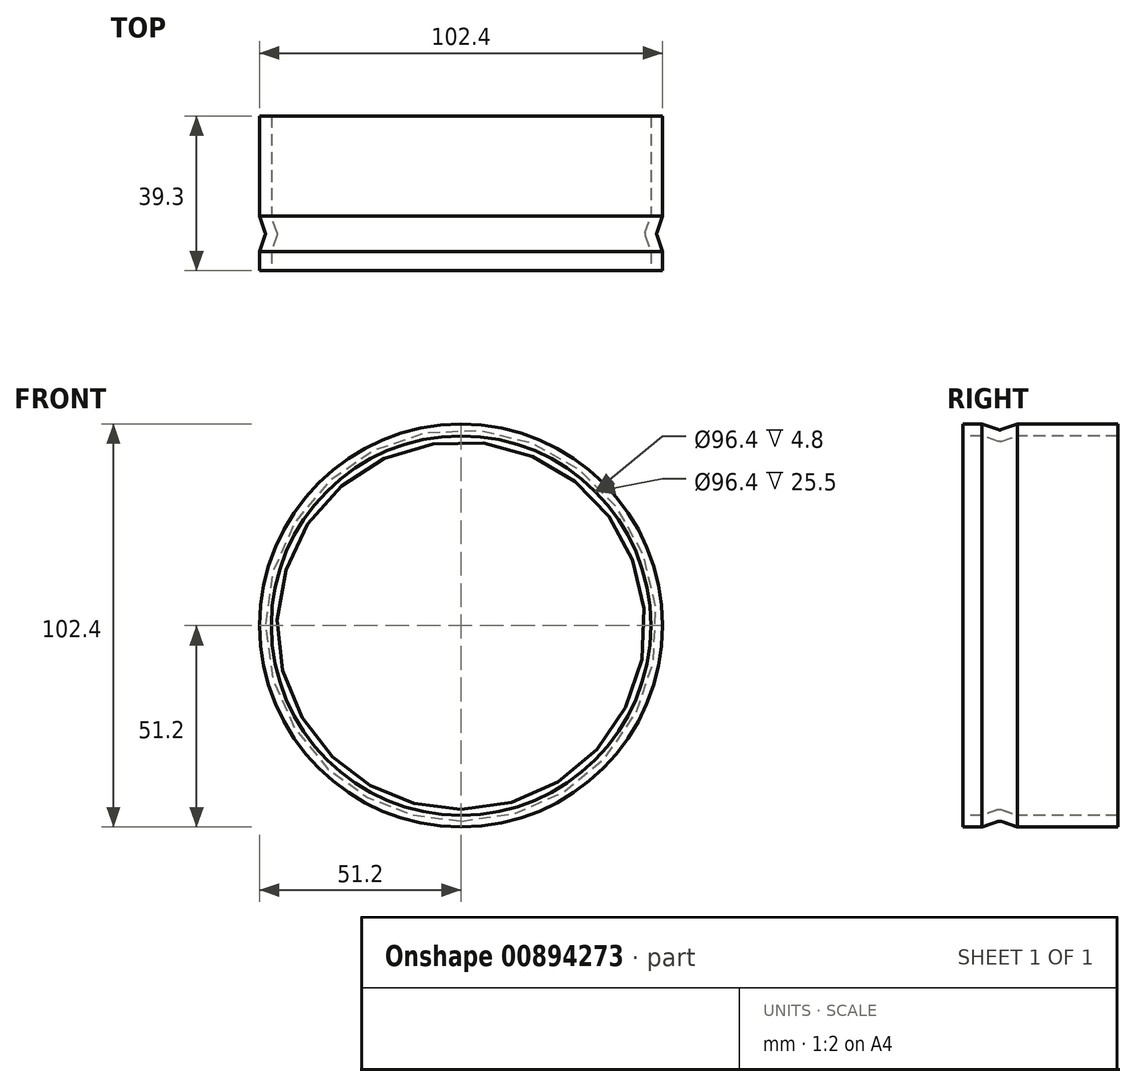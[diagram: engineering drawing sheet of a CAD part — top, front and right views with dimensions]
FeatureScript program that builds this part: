
annotation { "Feature Type Name" : "Feature", "Feature Type Description" : "" }
export const myFeature = defineFeature(function(context is Context, id is Id, definition is map)
    precondition{}
    {
        {
            var Q0;
            Q0=qCreatedBy(makeId("Right.planeOp"),FACE);
            var sketch = newSketch(context, id + "F0", { "sketchPlane" : qUnion([Q0])});
            skLineSegment(sketch, "E0", {"start": v(0, 0) * mm, "end": v(0, 48.2) * mm, "construction": true});
            skLineSegment(sketch, "E1", {"start": v(0, 0) * mm, "end": v(39.3, 0) * mm});
            skLineSegment(sketch, "E2", {"start": v(0, 48.2) * mm, "end": v(4.8, 48.2) * mm});
            skLineSegment(sketch, "E3", {"start": v(13.8, 48.2) * mm, "end": v(39.3, 48.2) * mm});
            skLineSegment(sketch, "E4", {"start": v(0, 48.2) * mm, "end": v(0, 51.2) * mm});
            skLineSegment(sketch, "E5", {"start": v(0, 51.2) * mm, "end": v(4.8, 51.2) * mm});
            skLineSegment(sketch, "E6", {"start": v(13.8, 51.2) * mm, "end": v(39.3, 51.2) * mm});
            skLineSegment(sketch, "E7", {"start": v(39.3, 51.2) * mm, "end": v(39.3, 48.2) * mm});
            skLineSegment(sketch, "E8", {"start": v(4.8, 48.2) * mm, "end": v(8.97, 46.76) * mm});
            skLineSegment(sketch, "E9", {"start": v(9.63, 46.76) * mm, "end": v(13.8, 48.2) * mm});
            skLineSegment(sketch, "E10", {"start": v(4.8, 51.2) * mm, "end": v(8.97, 49.76) * mm});
            skLineSegment(sketch, "E11", {"start": v(9.63, 49.76) * mm, "end": v(13.8, 51.2) * mm});
            skPoint(sketch, "E12.visualSharp", {"position": v(9.3, 49.64) * mm});
            skArc(sketch, "E12.filletArc", {"start": v(8.97, 49.76) * mm, "mid": v(9.3, 49.7) * mm, "end": v(9.63, 49.76) * mm});
            skPoint(sketch, "E13.visualSharp", {"position": v(9.3, 46.64) * mm});
            skArc(sketch, "E13.filletArc", {"start": v(8.97, 46.76) * mm, "mid": v(9.3, 46.7) * mm, "end": v(9.63, 46.76) * mm});
            skSolve(sketch);
        }
        {
            var Q0;
            Q0 = qSketchRegion(id + "F0", true);
            var Q1;
            Q1=sQuery(id+"F0.wireOp",EDGE,"E1");
            revolve(context, id + "F1", {"surfaceOperationType" : NewSurfaceOperationType.NEW, "entities" : qUnion([Q0]), "axis" : qUnion([Q1]), "revolveType" : RevolveType.FULL});
        }
    });
